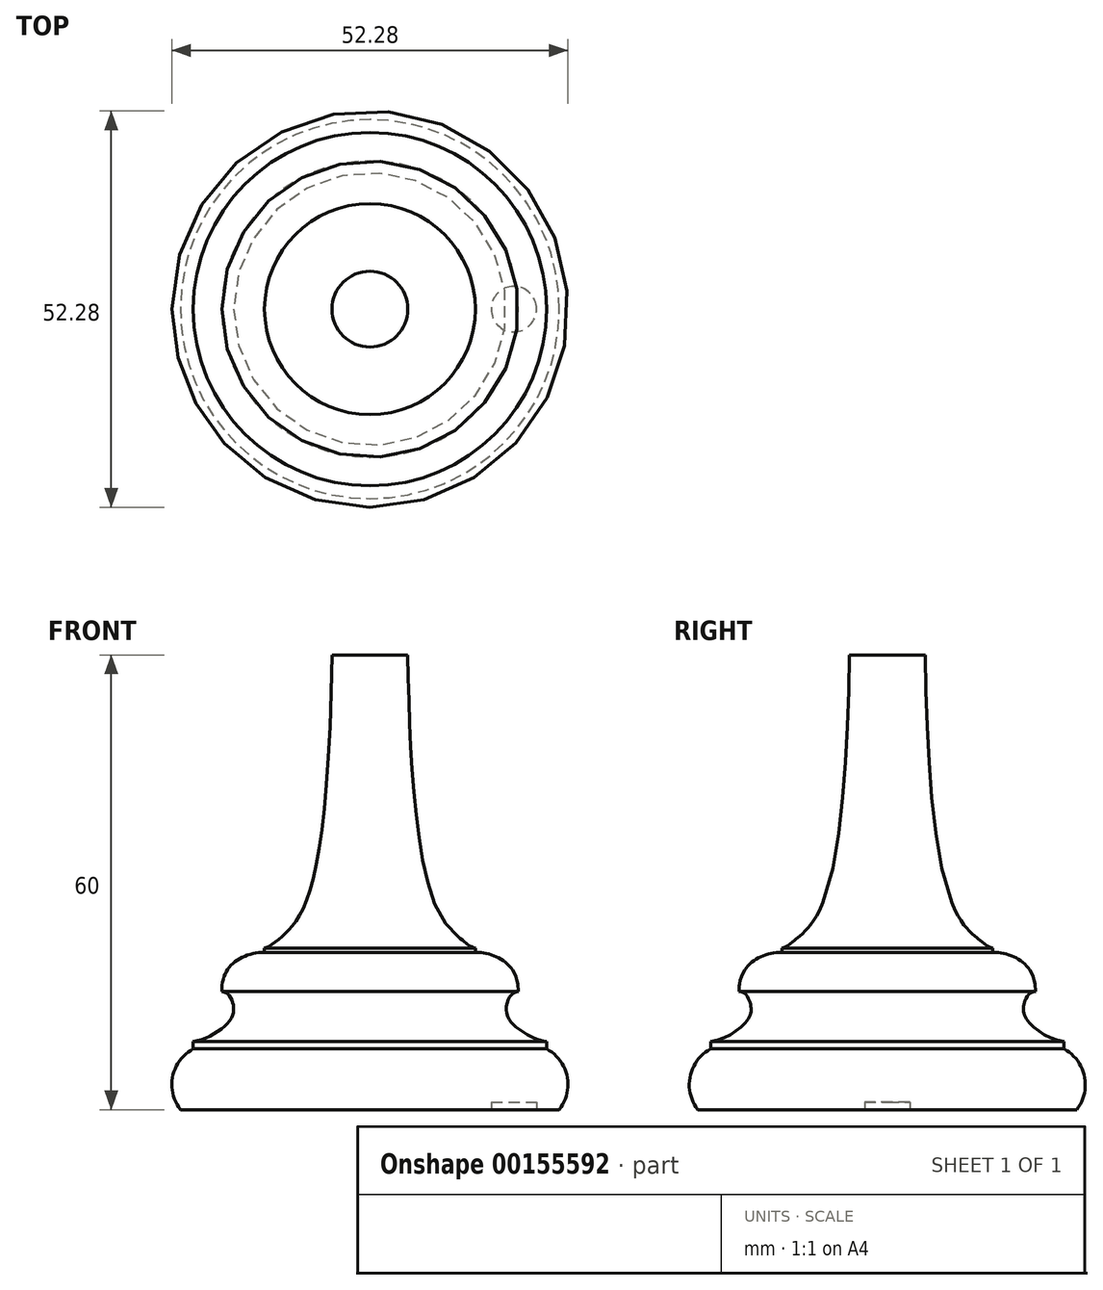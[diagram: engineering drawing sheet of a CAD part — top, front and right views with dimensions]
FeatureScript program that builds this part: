
annotation { "Feature Type Name" : "Feature", "Feature Type Description" : "" }
export const myFeature = defineFeature(function(context is Context, id is Id, definition is map)
    precondition{}
    {
        {
            var Q0;
            Q0=qCreatedBy(makeId("Front.planeOp"),FACE);
            var sketch = newSketch(context, id + "F0", { "sketchPlane" : qUnion([Q0])});
            skCircle(sketch, "E0", {"center": v(0, 0) * mm, "radius": 25 * mm});
            skLineSegment(sketch, "E1", {"start": v(-25, 0) * mm, "end": v(25, 0) * mm});
            skCircle(sketch, "E2", {"center": v(-20.77, 3.3) * mm, "radius": 5.37 * mm});
            skLineSegment(sketch, "E3", {"start": v(-23.32, 8.02) * mm, "end": v(-23.32, 9) * mm});
            skFitSpline(sketch, "E4", {"points": [v(-23.32, 9) * mm, v(-18.45, 11.82) * mm, v(-18.08, 14.03) * mm, v(-19.55, 15.58) * mm], "startDerivative": vector(12.37, 1.29) * mm, "endDerivative": vector(-9.98, 0.9) * mm});
            skFitSpline(sketch, "E5", {"points": [v(-19.55, 15.58) * mm, v(-17.95, 19.4) * mm, v(-13.91, 20.77) * mm], "startDerivative": vector(-0.25, 10.24) * mm, "endDerivative": vector(8.8, -0.08) * mm});
            skLineSegment(sketch, "E6", {"start": v(-13.91, 20.77) * mm, "end": v(-13.91, 21.28) * mm});
            skLineSegment(sketch, "E7", {"start": v(0, 0) * mm, "end": v(0, 60) * mm});
            skFitSpline(sketch, "E8", {"points": [v(-13.91, 21.28) * mm, v(-11.7, 22.8) * mm, v(-5, 60) * mm], "startDerivative": vector(12.26, 4.56) * mm, "endDerivative": vector(1.86, 120.56) * mm});
            skLineSegment(sketch, "E9", {"start": v(-5, 60) * mm, "end": v(0, 60) * mm});
            skSolve(sketch);
        }
        {
            var Q0;
            {var subQ0=sQuery(id+"F0.wireOp",EDGE,"E3");Q0=makeQuery(id+"F0.imprint","IMPRINT",FACE,{"disambiguationData":[TD([[makeQuery(id+"F0.imprint","IMPRINT",EDGE,{"derivedFrom":subQ0}),-1.0]])]});}
            var Q1;
            {var subQ4=sQuery(id+"F0.wireOp",EDGE,"E6");Q1=makeQuery(id+"F0.imprint","IMPRINT",FACE,{"disambiguationData":[TD([[makeQuery(id+"F0.imprint","IMPRINT",EDGE,{"derivedFrom":subQ4}),-1.0]])]});}
            var Q2;
            {var subQ0=sQuery(id+"F0.wireOp",EDGE,"E5");Q2=makeQuery(id+"F0.imprint","IMPRINT",FACE,{"disambiguationData":[TD([[makeQuery(id+"F0.imprint","IMPRINT",EDGE,{"derivedFrom":subQ0}),-1.0]])]});}
            var Q3;
            {var subQ0=sQuery(id+"F0.wireOp",EDGE,"E2");var subQ6=makeQuery(id+"F0.imprint","INTERSECT",VERTEX,{"derivedFrom":[subQ0,sQuery(id+"F0.wireOp",EDGE,"E3")]});Q3=makeQuery(id+"F0.imprint","IMPRINT",FACE,{"disambiguationData":[TD([[makeQuery(id+"F0.imprint","IMPRINT",EDGE,{"disambiguationData":[TD([[subQ6,-1.0]])],"derivedFrom":subQ0}),1.0]])]});}
            var Q4;
            {var subQ0=sQuery(id+"F0.wireOp",EDGE,"E2");var subQ1=sQuery(id+"F0.wireOp",EDGE,"E0");var subQ3=makeQuery(id+"F0.imprint","INTERSECT",VERTEX,{"derivedFrom":[subQ1,subQ0]});Q4=makeQuery(id+"F0.imprint","IMPRINT",FACE,{"disambiguationData":[TD([[makeQuery(id+"F0.imprint","IMPRINT",EDGE,{"disambiguationData":[TD([[subQ3,-1.0]])],"derivedFrom":subQ1}),-1.0]])]});}
            var Q5;
            Q5=sQuery(id+"F0.wireOp",EDGE,"E7");
            revolve(context, id + "F1", {"entities" : qUnion([Q0, Q1, Q2, Q3, Q4]), "axis" : qUnion([Q5]), "revolveType" : RevolveType.FULL});
        }
        {
            var Q0;
            Q0=makeQuery(id+"F1.opRevolve","SWEPT_FACE",FACE,{"disambiguationData":[OSD([sQuery(id+"F0.wireOp",EDGE,"E1")])]});
            var sketch = newSketch(context, id + "F2", { "sketchPlane" : qUnion([Q0])});
            skCircle(sketch, "E10", {"center": v(19, 0) * mm, "radius": 3 * mm});
            skSolve(sketch);
        }
        {
            var Q0;
            Q0=makeQuery(id+"F2.imprint","IMPRINT",FACE,{"disambiguationData":[TD([[makeQuery(id+"F2.imprint","IMPRINT",EDGE,{"derivedFrom":sQuery(id+"F2.wireOp",EDGE,"E10")}),1.0]])]});
            extrude(context, id + "F3", {"entities" : qUnion([Q0]), "operationType" : NewBodyOperationType.REMOVE, "oppositeDirection" : true, "depth" : 1 * mm});
        }
    });
